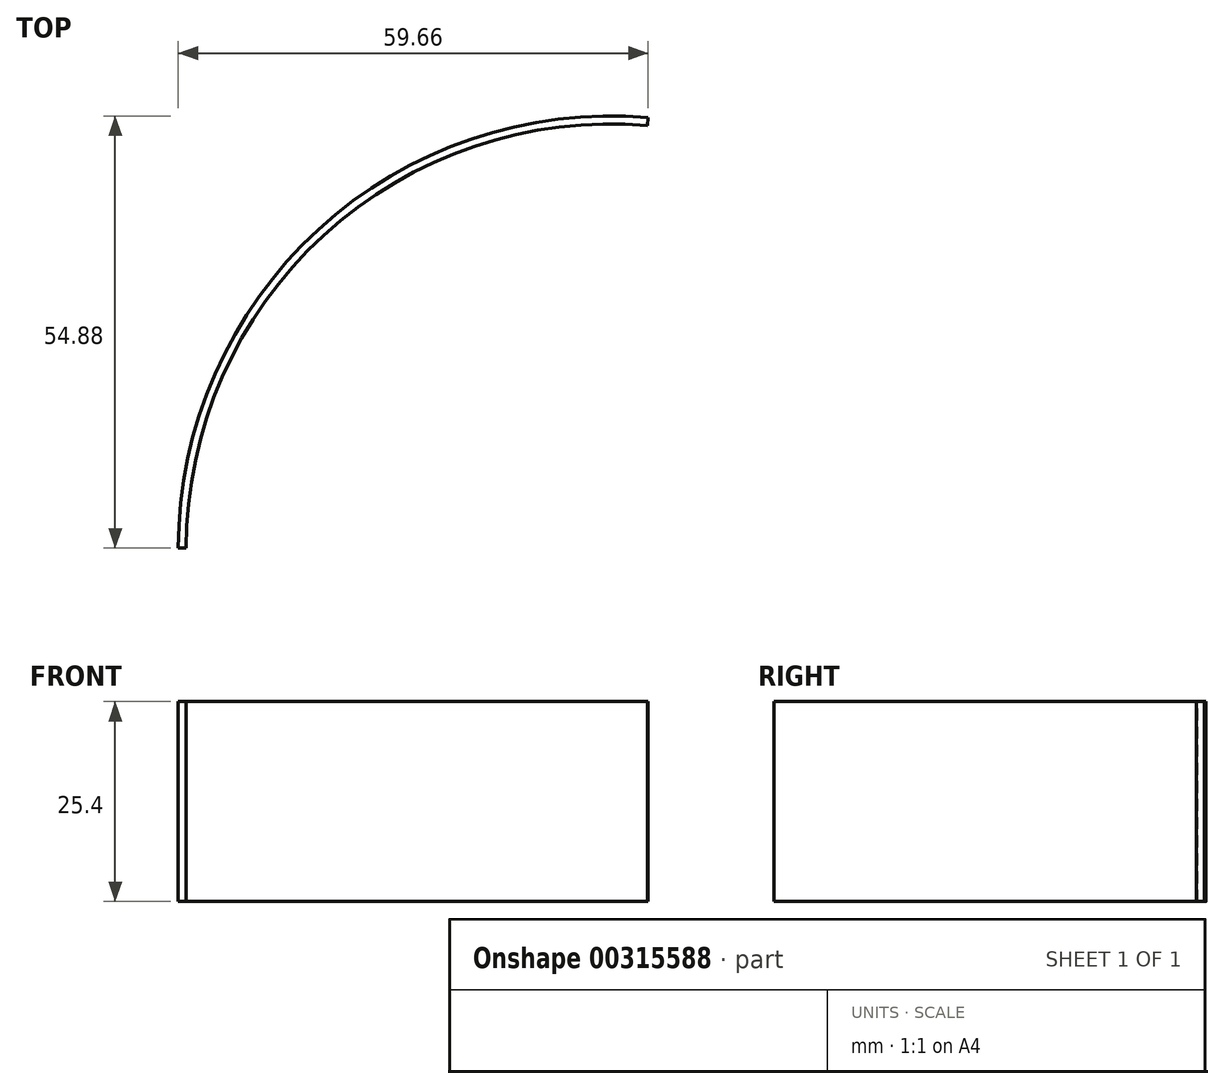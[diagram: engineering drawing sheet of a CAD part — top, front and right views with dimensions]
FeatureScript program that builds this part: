
annotation { "Feature Type Name" : "Feature", "Feature Type Description" : "" }
export const myFeature = defineFeature(function(context is Context, id is Id, definition is map)
    precondition{}
    {
        {
            var Q0;
            Q0=qCreatedBy(makeId("Front.planeOp"),FACE);
            var sketch = newSketch(context, id + "F0", { "sketchPlane" : qUnion([Q0])});
            skLineSegment(sketch, "E0.bottom", {"start": v(-54.88, 0) * mm, "end": v(-53.88, 0) * mm});
            skLineSegment(sketch, "E0.top", {"start": v(-54.88, 25.4) * mm, "end": v(-53.88, 25.4) * mm});
            skLineSegment(sketch, "E0.left", {"start": v(-54.88, 0) * mm, "end": v(-54.88, 25.4) * mm});
            skLineSegment(sketch, "E0.right", {"start": v(-53.88, 0) * mm, "end": v(-53.88, 25.4) * mm});
            skLineSegment(sketch, "E1", {"start": v(0, 26.08) * mm, "end": v(0, 0) * mm});
            skSolve(sketch);
        }
        {
            var Q0;
            Q0=makeQuery(id+"F0.imprint","IMPRINT",FACE,{"disambiguationData":[TD([[makeQuery(id+"F0.imprint","IMPRINT",EDGE,{"derivedFrom":sQuery(id+"F0.wireOp",EDGE,"E0.bottom")}),1.0]])]});
            var Q1;
            Q1=sQuery(id+"F0.wireOp",EDGE,"E1");
            revolve(context, id + "F1", {"entities" : qUnion([Q0]), "axis" : qUnion([Q1]), "revolveType" : RevolveType.ONE_DIRECTION, "angle" : 95 * degree});
        }
    });
